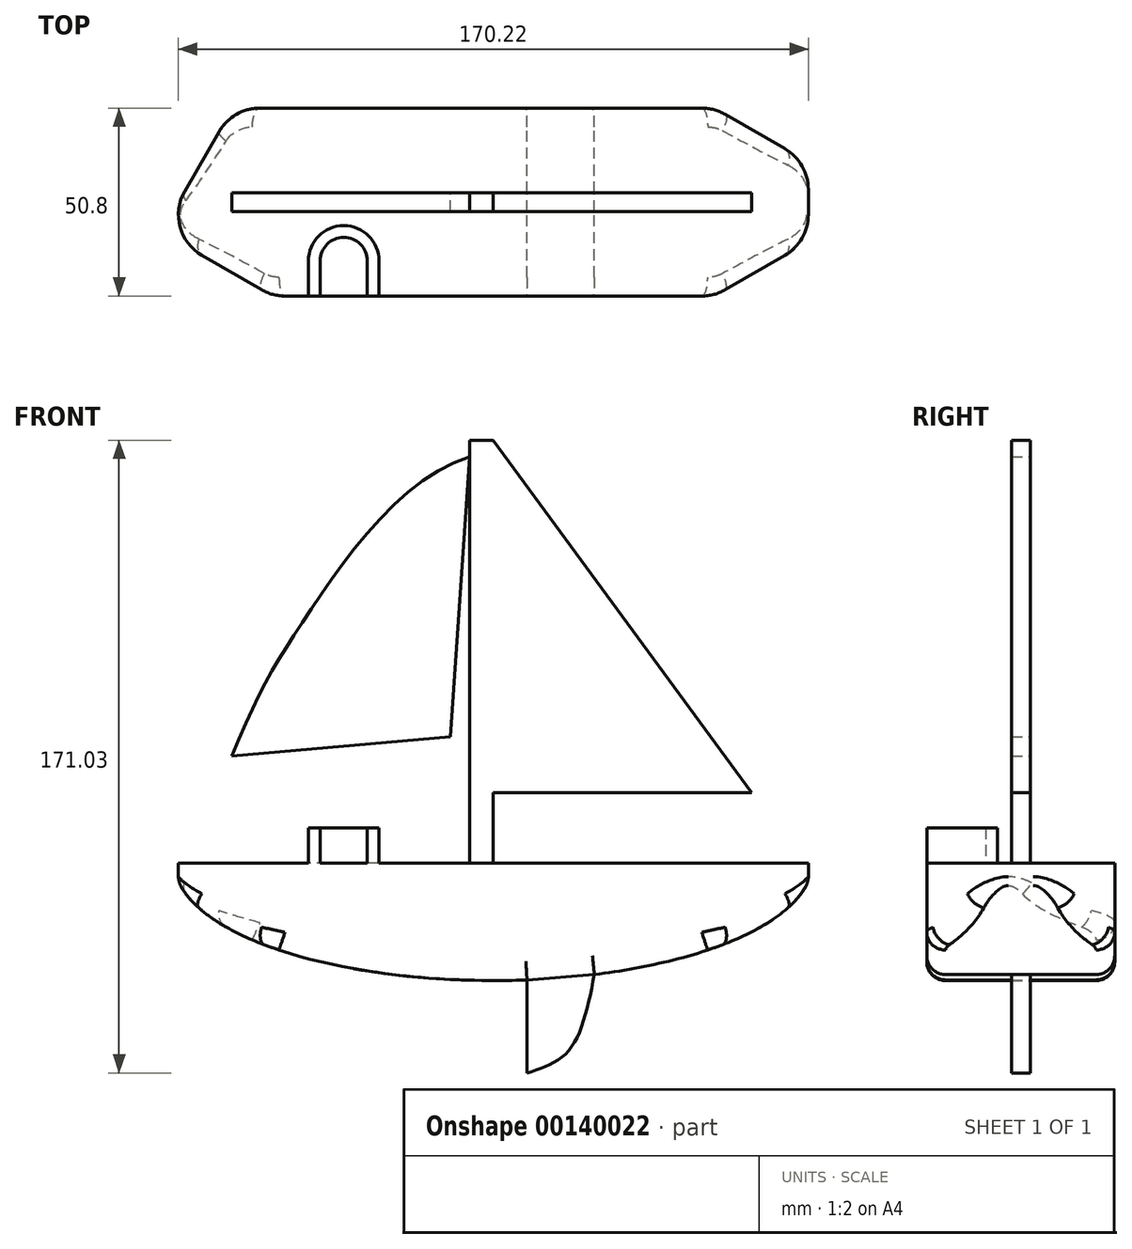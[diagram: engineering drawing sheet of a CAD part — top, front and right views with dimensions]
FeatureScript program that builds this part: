
annotation { "Feature Type Name" : "Feature", "Feature Type Description" : "" }
export const myFeature = defineFeature(function(context is Context, id is Id, definition is map)
    precondition{}
    {
        {
            var Q0;
            Q0=qCreatedBy(makeId("Front.planeOp"),FACE);
            var sketch = newSketch(context, id + "F0", { "sketchPlane" : qUnion([Q0])});
            skEllipticalArc(sketch, "E0", {});
            skLineSegment(sketch, "E1", {"start": v(-85.1, 0) * mm, "end": v(-6.35, 0) * mm, "construction": true});
            skLineSegment(sketch, "E2", {"start": v(-85.1, 0) * mm, "end": v(-6.35, 0) * mm});
            skLineSegment(sketch, "E3", {"start": v(0, 0) * mm, "end": v(0, -31.75) * mm, "construction": true});
            skLineSegment(sketch, "E4", {"start": v(0, 0) * mm, "end": v(0, 19.05) * mm});
            skLineSegment(sketch, "E5", {"start": v(0, 114.3) * mm, "end": v(-6.35, 114.3) * mm});
            skLineSegment(sketch, "E6", {"start": v(-6.35, 114.3) * mm, "end": v(-6.35, 0) * mm});
            skLineSegment(sketch, "E7", {"start": v(0, 114.3) * mm, "end": v(69.85, 19.05) * mm});
            skLineSegment(sketch, "E8", {"start": v(69.85, 19.05) * mm, "end": v(0, 19.05) * mm});
            skEllipticalArc(sketch, "E9.trimOffspring", {});
            skLineSegment(sketch, "E10.trimOffspring", {"start": v(0, 0) * mm, "end": v(85.1, 0) * mm, "construction": true});
            skLineSegment(sketch, "E11.trimOffspring", {"start": v(0, 0) * mm, "end": v(85.1, 0) * mm});
            skLineSegment(sketch, "E12", {"start": v(-85.1, -4.8) * mm, "end": v(-85.1, 0) * mm});
            skLineSegment(sketch, "E13.MirrorCS", {"start": v(85.1, -4.8) * mm, "end": v(85.1, 0) * mm});
            skPoint(sketch, "E14.start.orphan", {"position": v(-96.52, 0) * mm});
            skPoint(sketch, "E15.orphan", {"position": v(-86.1, 0) * mm});
            skPoint(sketch, "E16.start.orphan", {"position": v(96.52, 0) * mm});
            skPoint(sketch, "E17.orphan", {"position": v(86.1, 0) * mm});
            skLineSegment(sketch, "E18", {"start": v(-70.7, 28.95) * mm, "end": v(-11.56, 34.2) * mm});
            skLineSegment(sketch, "E19", {"start": v(-11.56, 34.2) * mm, "end": v(-6.35, 109.84) * mm});
            skFitSpline(sketch, "E20", {"points": [v(-70.7, 28.95) * mm, v(-50.6, 66.66) * mm, v(-6.35, 109.84) * mm], "startDerivative": vector(45.7, 111.82) * mm, "endDerivative": vector(101.73, 29.56) * mm});
            skLineSegment(sketch, "E21", {"start": v(9.07, -31.57) * mm, "end": v(9.07, -56.73) * mm});
            skFitSpline(sketch, "E22", {"points": [v(9.07, -56.73) * mm, v(20.32, -50.7) * mm, v(27.28, -30.11) * mm], "startDerivative": vector(28.97, 9) * mm, "endDerivative": vector(8.33, 43.1) * mm});
            skEllipticalArc(sketch, "E23.trimOffspring", {});
            const initialGuessF0  = {"E0": [0, 0, 1, 0, 0.08609891581009588, 0.03175, 3.293558796951954, 4.712289809308396], "E9.trimOffspring": [0, 0, 1, 0, 0.08609891581009588, 0.03175, 4.076115573731887, 4.817965946805809], "E23.trimOffspring": [0, 0, 1, 0, 0.08609891581009588, 0.03175, 5.034846905697643, 6.1312191638174225]};
            skSetInitialGuess(sketch, initialGuessF0);
            skSolve(sketch);
        }
        {
            var Q0;
            Q0 = qSketchRegion(id + "F0", true);
            extrude(context, id + "F1", {"entities" : qUnion([Q0]), "depth" : 2.54 * mm, "hasSecondDirection" : true, "secondDirectionOppositeDirection" : true, "secondDirectionDepth" : 2.54 * mm});
        }
        {
            var Q0;
            Q0=qCreatedBy(makeId("Front.planeOp"),FACE);
            var sketch = newSketch(context, id + "F2", { "sketchPlane" : qUnion([Q0])});
            skLineSegment(sketch, "E24.0.0", {"start": v(-85.1, 0) * mm, "end": v(-85.1, -4.8) * mm});
            skEllipticalArc(sketch, "E24.0.1", {});
            skEllipticalArc(sketch, "E24.0.4", {});
            skLineSegment(sketch, "E24.0.5", {"start": v(85.1, -4.8) * mm, "end": v(85.1, 0) * mm});
            skLineSegment(sketch, "E24.0.6", {"start": v(85.1, 0) * mm, "end": v(0, 0) * mm});
            skLineSegment(sketch, "E24.0.12", {"start": v(-6.35, 0) * mm, "end": v(-85.1, 0) * mm});
            skLineSegment(sketch, "E25", {"start": v(-6.35, 0) * mm, "end": v(0, 0) * mm});
            skPoint(sketch, "E24.0.9.start.orphan", {"position": v(69.85, 19.05) * mm});
            skPoint(sketch, "E24.0.10.end.orphan", {"position": v(-6.35, 114.3) * mm});
            skPoint(sketch, "E24.0.10.start.orphan", {"position": v(0, 114.3) * mm});
            skPoint(sketch, "E24.0.3.start.orphan", {"position": v(9.07, -56.73) * mm});
            skPoint(sketch, "E24.0.7.end.orphan", {"position": v(0, 19.05) * mm});
            skLineSegment(sketch, "E26", {"start": v(9.07, -31.57) * mm, "end": v(27.28, -30.11) * mm});
            const initialGuessF2  = {"E24.0.1": [0, 0, 1, 0, 0.08609891581009588, 0.03175, 3.293558796951954, 4.817965946805809], "E24.0.4": [0, 0, 1, 0, 0.08609891581009588, 0.03175, 5.034846905697643, 6.1312191638174225], "E24.0.1": [0, 0, 1, 0, 0.08609891581009588, 0.03175, 3.293558796951954, 4.817965946805809], "E24.0.4": [0, 0, 1, 0, 0.08609891581009588, 0.03175, 5.034846905697643, 6.1312191638174225]};
            skSetInitialGuess(sketch, initialGuessF2);
            skSolve(sketch);
        }
        {
            var Q0;
            Q0 = qSketchRegion(id + "F2", true);
            extrude(context, id + "F3", {"entities" : qUnion([Q0]), "operationType" : NewBodyOperationType.ADD, "depth" : 25.4 * mm, "hasSecondDirection" : true, "secondDirectionOppositeDirection" : true, "secondDirectionDepth" : 25.4 * mm});
        }
        {
            var Q0;
            Q0=makeQuery(id+"F3.opExtrude","CAP_EDGE",EDGE,{"disambiguationData":[OSD([sQuery(id+"F2.wireOp",EDGE,"E24.0.5")])],"isStart":false});
            var Q1;
            Q1=makeQuery(id+"F3.opExtrude","CAP_EDGE",EDGE,{"disambiguationData":[OSD([sQuery(id+"F2.wireOp",EDGE,"E24.0.5")])],"isStart":true});
            var Q2;
            Q2=makeQuery(id+"F3.opExtrude","CAP_EDGE",EDGE,{"disambiguationData":[OSD([sQuery(id+"F2.wireOp",EDGE,"E24.0.0")])],"isStart":false});
            var Q3;
            Q3=makeQuery(id+"F3.opExtrude","CAP_EDGE",EDGE,{"disambiguationData":[OSD([sQuery(id+"F2.wireOp",EDGE,"E24.0.0")])],"isStart":true});
            chamfer(context, id + "F4", {"entities" : qUnion([Q0, Q1, Q2, Q3]), "chamferType" : ChamferType.OFFSET_ANGLE, "width" : 25.4 * mm, "oppositeDirection" : false, "angle" : 30 * degree, "tangentPropagation" : true});
        }
        {
            var Q0;
            {var subQ0=sQuery(id+"F2.wireOp",EDGE,"E24.0.0");Q0=makeQuery(id+"F4.opChamfer","BLEND_EDGE",EDGE,{"blendedFrom":[makeQuery(id+"F3.opExtrude","CAP_EDGE",EDGE,{"disambiguationData":[OSD([subQ0])],"isStart":false}),makeQuery(id+"F3.opExtrude","CAP_FACE",FACE,{"disambiguationData":[OSD([subQ0,sQuery(id+"F2.wireOp",EDGE,"E24.0.5"),sQuery(id+"F2.wireOp",EDGE,"E24.0.6"),sQuery(id+"F2.wireOp",EDGE,"E24.0.12"),sQuery(id+"F2.wireOp",EDGE,"E25"),sQuery(id+"F2.wireOp",EDGE,"E24.0.1"),sQuery(id+"F2.wireOp",EDGE,"E24.0.4"),sQuery(id+"F2.wireOp",EDGE,"E26")])],"isStart":false})],"blendedInto":[makeQuery(id+"F3.opExtrude","CAP_FACE",FACE,{"disambiguationData":[OSD([subQ0,sQuery(id+"F2.wireOp",EDGE,"E24.0.5"),sQuery(id+"F2.wireOp",EDGE,"E24.0.6"),sQuery(id+"F2.wireOp",EDGE,"E24.0.12"),sQuery(id+"F2.wireOp",EDGE,"E25"),sQuery(id+"F2.wireOp",EDGE,"E24.0.1"),sQuery(id+"F2.wireOp",EDGE,"E24.0.4"),sQuery(id+"F2.wireOp",EDGE,"E26")])],"isStart":false})]});}
            var Q1;
            {var subQ0=sQuery(id+"F2.wireOp",EDGE,"E24.0.5");Q1=makeQuery(id+"F4.opChamfer","BLEND_EDGE",EDGE,{"blendedFrom":[makeQuery(id+"F3.opExtrude","CAP_EDGE",EDGE,{"disambiguationData":[OSD([subQ0])],"isStart":false}),makeQuery(id+"F3.opExtrude","CAP_FACE",FACE,{"disambiguationData":[OSD([sQuery(id+"F2.wireOp",EDGE,"E24.0.0"),subQ0,sQuery(id+"F2.wireOp",EDGE,"E24.0.6"),sQuery(id+"F2.wireOp",EDGE,"E24.0.12"),sQuery(id+"F2.wireOp",EDGE,"E25"),sQuery(id+"F2.wireOp",EDGE,"E24.0.1"),sQuery(id+"F2.wireOp",EDGE,"E24.0.4"),sQuery(id+"F2.wireOp",EDGE,"E26")])],"isStart":false})],"blendedInto":[makeQuery(id+"F3.opExtrude","CAP_FACE",FACE,{"disambiguationData":[OSD([sQuery(id+"F2.wireOp",EDGE,"E24.0.0"),subQ0,sQuery(id+"F2.wireOp",EDGE,"E24.0.6"),sQuery(id+"F2.wireOp",EDGE,"E24.0.12"),sQuery(id+"F2.wireOp",EDGE,"E25"),sQuery(id+"F2.wireOp",EDGE,"E24.0.1"),sQuery(id+"F2.wireOp",EDGE,"E24.0.4"),sQuery(id+"F2.wireOp",EDGE,"E26")])],"isStart":false})]});}
            var Q2;
            {var subQ0=sQuery(id+"F2.wireOp",EDGE,"E24.0.5");Q2=makeQuery(id+"F4.opChamfer","BLEND_EDGE",EDGE,{"blendedFrom":[makeQuery(id+"F3.opExtrude","CAP_EDGE",EDGE,{"disambiguationData":[OSD([subQ0])],"isStart":false}),makeQuery(id+"F3.boolean.opBoolean","MERGE",FACE,{"derivedFrom":[makeQuery(id+"F1.opExtrude","SWEPT_FACE",FACE,{"disambiguationData":[OSD([sQuery(id+"F0.wireOp",EDGE,"E13.MirrorCS")])]}),makeQuery(id+"F3.opExtrude","SWEPT_FACE",FACE,{"disambiguationData":[OSD([subQ0])]})]})],"blendedInto":[makeQuery(id+"F3.boolean.opBoolean","MERGE",FACE,{"derivedFrom":[makeQuery(id+"F1.opExtrude","SWEPT_FACE",FACE,{"disambiguationData":[OSD([sQuery(id+"F0.wireOp",EDGE,"E13.MirrorCS")])]}),makeQuery(id+"F3.opExtrude","SWEPT_FACE",FACE,{"disambiguationData":[OSD([subQ0])]})]})]});}
            var Q3;
            {var subQ0=sQuery(id+"F2.wireOp",EDGE,"E24.0.5");Q3=makeQuery(id+"F4.opChamfer","BLEND_EDGE",EDGE,{"blendedFrom":[makeQuery(id+"F3.opExtrude","CAP_EDGE",EDGE,{"disambiguationData":[OSD([subQ0])],"isStart":true}),makeQuery(id+"F3.boolean.opBoolean","MERGE",FACE,{"derivedFrom":[makeQuery(id+"F1.opExtrude","SWEPT_FACE",FACE,{"disambiguationData":[OSD([sQuery(id+"F0.wireOp",EDGE,"E13.MirrorCS")])]}),makeQuery(id+"F3.opExtrude","SWEPT_FACE",FACE,{"disambiguationData":[OSD([subQ0])]})]})],"blendedInto":[makeQuery(id+"F3.boolean.opBoolean","MERGE",FACE,{"derivedFrom":[makeQuery(id+"F1.opExtrude","SWEPT_FACE",FACE,{"disambiguationData":[OSD([sQuery(id+"F0.wireOp",EDGE,"E13.MirrorCS")])]}),makeQuery(id+"F3.opExtrude","SWEPT_FACE",FACE,{"disambiguationData":[OSD([subQ0])]})]})]});}
            var Q4;
            {var subQ0=sQuery(id+"F2.wireOp",EDGE,"E24.0.5");Q4=makeQuery(id+"F4.opChamfer","BLEND_EDGE",EDGE,{"blendedFrom":[makeQuery(id+"F3.opExtrude","CAP_EDGE",EDGE,{"disambiguationData":[OSD([subQ0])],"isStart":true}),makeQuery(id+"F3.opExtrude","CAP_FACE",FACE,{"disambiguationData":[OSD([sQuery(id+"F2.wireOp",EDGE,"E24.0.0"),subQ0,sQuery(id+"F2.wireOp",EDGE,"E24.0.6"),sQuery(id+"F2.wireOp",EDGE,"E24.0.12"),sQuery(id+"F2.wireOp",EDGE,"E25"),sQuery(id+"F2.wireOp",EDGE,"E24.0.1"),sQuery(id+"F2.wireOp",EDGE,"E24.0.4"),sQuery(id+"F2.wireOp",EDGE,"E26")])],"isStart":true})],"blendedInto":[makeQuery(id+"F3.opExtrude","CAP_FACE",FACE,{"disambiguationData":[OSD([sQuery(id+"F2.wireOp",EDGE,"E24.0.0"),subQ0,sQuery(id+"F2.wireOp",EDGE,"E24.0.6"),sQuery(id+"F2.wireOp",EDGE,"E24.0.12"),sQuery(id+"F2.wireOp",EDGE,"E25"),sQuery(id+"F2.wireOp",EDGE,"E24.0.1"),sQuery(id+"F2.wireOp",EDGE,"E24.0.4"),sQuery(id+"F2.wireOp",EDGE,"E26")])],"isStart":true})]});}
            var Q5;
            {var subQ0=sQuery(id+"F2.wireOp",EDGE,"E24.0.0");Q5=makeQuery(id+"F4.opChamfer","BLEND_EDGE",EDGE,{"blendedFrom":[makeQuery(id+"F3.opExtrude","CAP_EDGE",EDGE,{"disambiguationData":[OSD([subQ0])],"isStart":true}),makeQuery(id+"F3.boolean.opBoolean","MERGE",FACE,{"derivedFrom":[makeQuery(id+"F1.opExtrude","SWEPT_FACE",FACE,{"disambiguationData":[OSD([sQuery(id+"F0.wireOp",EDGE,"E12")])]}),makeQuery(id+"F3.opExtrude","SWEPT_FACE",FACE,{"disambiguationData":[OSD([subQ0])]})]})],"blendedInto":[makeQuery(id+"F3.boolean.opBoolean","MERGE",FACE,{"derivedFrom":[makeQuery(id+"F1.opExtrude","SWEPT_FACE",FACE,{"disambiguationData":[OSD([sQuery(id+"F0.wireOp",EDGE,"E12")])]}),makeQuery(id+"F3.opExtrude","SWEPT_FACE",FACE,{"disambiguationData":[OSD([subQ0])]})]})]});}
            var Q6;
            {var subQ0=sQuery(id+"F2.wireOp",EDGE,"E24.0.0");Q6=makeQuery(id+"F4.opChamfer","BLEND_EDGE",EDGE,{"blendedFrom":[makeQuery(id+"F3.opExtrude","CAP_EDGE",EDGE,{"disambiguationData":[OSD([subQ0])],"isStart":false}),makeQuery(id+"F3.boolean.opBoolean","MERGE",FACE,{"derivedFrom":[makeQuery(id+"F1.opExtrude","SWEPT_FACE",FACE,{"disambiguationData":[OSD([sQuery(id+"F0.wireOp",EDGE,"E12")])]}),makeQuery(id+"F3.opExtrude","SWEPT_FACE",FACE,{"disambiguationData":[OSD([subQ0])]})]})],"blendedInto":[makeQuery(id+"F3.boolean.opBoolean","MERGE",FACE,{"derivedFrom":[makeQuery(id+"F1.opExtrude","SWEPT_FACE",FACE,{"disambiguationData":[OSD([sQuery(id+"F0.wireOp",EDGE,"E12")])]}),makeQuery(id+"F3.opExtrude","SWEPT_FACE",FACE,{"disambiguationData":[OSD([subQ0])]})]})]});}
            var Q7;
            {var subQ0=sQuery(id+"F2.wireOp",EDGE,"E24.0.0");Q7=makeQuery(id+"F4.opChamfer","BLEND_EDGE",EDGE,{"blendedFrom":[makeQuery(id+"F3.opExtrude","CAP_EDGE",EDGE,{"disambiguationData":[OSD([subQ0])],"isStart":true}),makeQuery(id+"F3.opExtrude","CAP_FACE",FACE,{"disambiguationData":[OSD([subQ0,sQuery(id+"F2.wireOp",EDGE,"E24.0.5"),sQuery(id+"F2.wireOp",EDGE,"E24.0.6"),sQuery(id+"F2.wireOp",EDGE,"E24.0.12"),sQuery(id+"F2.wireOp",EDGE,"E25"),sQuery(id+"F2.wireOp",EDGE,"E24.0.1"),sQuery(id+"F2.wireOp",EDGE,"E24.0.4"),sQuery(id+"F2.wireOp",EDGE,"E26")])],"isStart":true})],"blendedInto":[makeQuery(id+"F3.opExtrude","CAP_FACE",FACE,{"disambiguationData":[OSD([subQ0,sQuery(id+"F2.wireOp",EDGE,"E24.0.5"),sQuery(id+"F2.wireOp",EDGE,"E24.0.6"),sQuery(id+"F2.wireOp",EDGE,"E24.0.12"),sQuery(id+"F2.wireOp",EDGE,"E25"),sQuery(id+"F2.wireOp",EDGE,"E24.0.1"),sQuery(id+"F2.wireOp",EDGE,"E24.0.4"),sQuery(id+"F2.wireOp",EDGE,"E26")])],"isStart":true})]});}
            fillet(context, id + "F5", {"entities" : qUnion([Q0, Q1, Q2, Q3, Q4, Q5, Q6, Q7]), "radius" : 12.7 * mm, "tangentPropagation" : true, "allowEdgeOverflow" : false});
        }
        {
            var Q0;
            Q0=qCreatedBy(makeId("Top.planeOp"),FACE);
            var sketch = newSketch(context, id + "F6", { "sketchPlane" : qUnion([Q0])});
            skLineSegment(sketch, "E27.top", {"start": v(-49.95, -25.4) * mm, "end": v(-46.78, -25.4) * mm});
            skLineSegment(sketch, "E27.left", {"start": v(-49.95, -15.88) * mm, "end": v(-49.95, -25.4) * mm});
            skLineSegment(sketch, "E27.right", {"start": v(-30.9, -15.87) * mm, "end": v(-30.9, -25.4) * mm});
            skLineSegment(sketch, "E28", {"start": v(-46.78, -15.88) * mm, "end": v(-46.78, -25.4) * mm});
            skLineSegment(sketch, "E29", {"start": v(-34.08, -15.88) * mm, "end": v(-34.08, -25.4) * mm});
            skLineSegment(sketch, "E30.trimOffspring", {"start": v(-34.08, -25.4) * mm, "end": v(-30.9, -25.4) * mm});
            skArc(sketch, "E31", {"start": v(-30.9, -15.87) * mm, "mid": v(-40.43, -6.35) * mm, "end": v(-49.95, -15.87) * mm});
            skPoint(sketch, "E31.centerSnap0", {"position": v(-46.78, -15.88) * mm});
            skPoint(sketch, "E27.bottom.start.orphan", {"position": v(-49.95, -6.35) * mm});
            skPoint(sketch, "E32.orphan", {"position": v(-46.78, -6.35) * mm});
            skPoint(sketch, "E33.orphan", {"position": v(-30.9, -6.35) * mm});
            skArc(sketch, "E34.0", {"start": v(-34.08, -15.88) * mm, "mid": v(-40.43, -9.53) * mm, "end": v(-46.78, -15.88) * mm});
            skSolve(sketch);
        }
        {
            var Q0;
            Q0 = qSketchRegion(id + "F6", true);
            extrude(context, id + "F7", {"entities" : qUnion([Q0]), "operationType" : NewBodyOperationType.ADD, "depth" : 9.52 * mm});
        }
        {
            var Q0;
            Q0=makeQuery(id+"F3.opExtrude","CAP_EDGE",EDGE,{"disambiguationData":[OSD([sQuery(id+"F2.wireOp",EDGE,"E24.0.1")])],"isStart":false});
            var Q1;
            Q1=makeQuery(id+"F4.opChamfer","BLEND_EDGE",EDGE,{"blendedFrom":[makeQuery(id+"F3.opExtrude","CAP_EDGE",EDGE,{"disambiguationData":[OSD([sQuery(id+"F2.wireOp",EDGE,"E24.0.5")])],"isStart":false}),makeQuery(id+"F3.boolean.opBoolean","MERGE",FACE,{"derivedFrom":[makeQuery(id+"F1.opExtrude","SWEPT_FACE",FACE,{"disambiguationData":[OSD([sQuery(id+"F0.wireOp",EDGE,"E23.trimOffspring")])]}),makeQuery(id+"F3.opExtrude","SWEPT_FACE",FACE,{"disambiguationData":[OSD([sQuery(id+"F2.wireOp",EDGE,"E24.0.4")])]})]})],"blendedInto":[makeQuery(id+"F3.boolean.opBoolean","MERGE",FACE,{"derivedFrom":[makeQuery(id+"F1.opExtrude","SWEPT_FACE",FACE,{"disambiguationData":[OSD([sQuery(id+"F0.wireOp",EDGE,"E23.trimOffspring")])]}),makeQuery(id+"F3.opExtrude","SWEPT_FACE",FACE,{"disambiguationData":[OSD([sQuery(id+"F2.wireOp",EDGE,"E24.0.4")])]})]})]});
            fillet(context, id + "F8", {"entities" : qUnion([Q0, Q1]), "radius" : 5.08 * mm, "tangentPropagation" : true, "allowEdgeOverflow" : false});
        }
    });
